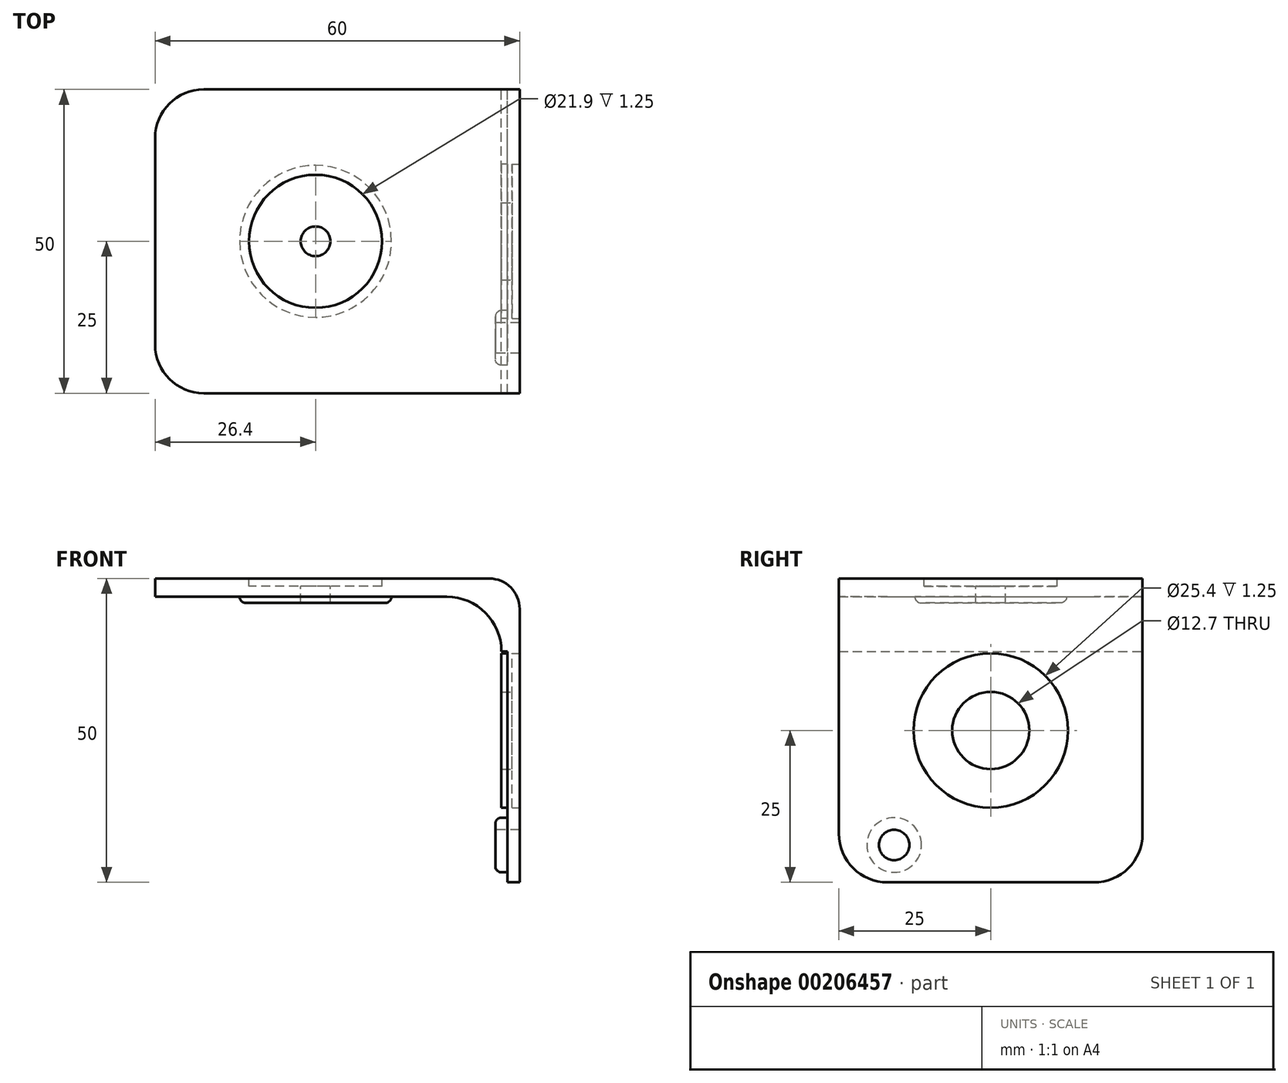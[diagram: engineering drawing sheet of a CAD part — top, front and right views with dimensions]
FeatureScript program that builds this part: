
annotation { "Feature Type Name" : "Feature", "Feature Type Description" : "" }
export const myFeature = defineFeature(function(context is Context, id is Id, definition is map)
    precondition{}
    {
        {
            var Q0;
            Q0=qCreatedBy(makeId("Front.planeOp"),FACE);
            var sketch = newSketch(context, id + "F0", { "sketchPlane" : qUnion([Q0])});
            skLineSegment(sketch, "E0.bottom", {"start": v(30, 25) * mm, "end": v(-30, 25) * mm});
            skLineSegment(sketch, "E0.top", {"start": v(30, -25) * mm, "end": v(27, -25) * mm});
            skLineSegment(sketch, "E0.left", {"start": v(30, 25) * mm, "end": v(30, -25) * mm});
            skLineSegment(sketch, "E0.right", {"start": v(-30, 25) * mm, "end": v(-30, 22) * mm});
            skPoint(sketch, "E0.middle", {"position": v(0, 0) * mm});
            skLineSegment(sketch, "E1", {"start": v(-30, 22) * mm, "end": v(18, 22) * mm});
            skLineSegment(sketch, "E2", {"start": v(27, 13) * mm, "end": v(27, -25) * mm});
            skPoint(sketch, "E3.orphan", {"position": v(-30, -25) * mm});
            skPoint(sketch, "E4.visualSharp", {"position": v(27, 22) * mm});
            skArc(sketch, "E4.filletArc", {"start": v(27, 13) * mm, "mid": v(24.36, 19.36) * mm, "end": v(18, 22) * mm});
            skSolve(sketch);
        }
        {
            var Q0;
            Q0=makeQuery(id+"F0.imprint","IMPRINT",FACE,{"disambiguationData":[TD([[makeQuery(id+"F0.imprint","IMPRINT",EDGE,{"derivedFrom":sQuery(id+"F0.wireOp",EDGE,"E0.bottom")}),1.0]])]});
            extrude(context, id + "F1", {"entities" : qUnion([Q0]), "endBound" : BoundingType.SYMMETRIC, "depth" : 50 * mm});
        }
        {
            var Q0;
            Q0=makeQuery(id+"F1.opExtrude","CAP_EDGE",EDGE,{"disambiguationData":[OSD([sQuery(id+"F0.wireOp",EDGE,"E0.right")])],"isStart":false});
            var Q1;
            Q1=makeQuery(id+"F1.opExtrude","CAP_EDGE",EDGE,{"disambiguationData":[OSD([sQuery(id+"F0.wireOp",EDGE,"E0.right")])],"isStart":true});
            var Q2;
            Q2=makeQuery(id+"F1.opExtrude","CAP_EDGE",EDGE,{"disambiguationData":[OSD([sQuery(id+"F0.wireOp",EDGE,"E0.top")])],"isStart":true});
            var Q3;
            Q3=makeQuery(id+"F1.opExtrude","CAP_EDGE",EDGE,{"disambiguationData":[OSD([sQuery(id+"F0.wireOp",EDGE,"E0.top")])],"isStart":false});
            fillet(context, id + "F2", {"entities" : qUnion([Q0, Q1, Q2, Q3]), "radius" : 8 * mm, "tangentPropagation" : true, "allowEdgeOverflow" : false});
        }
        {
            var Q0;
            Q0=makeQuery(id+"F1.opExtrude","SWEPT_FACE",FACE,{"disambiguationData":[OSD([sQuery(id+"F0.wireOp",EDGE,"E0.bottom")])]});
            var sketch = newSketch(context, id + "F3", { "sketchPlane" : qUnion([Q0])});
            skCircle(sketch, "E5", {"center": v(-3.6, 0) * mm, "radius": 10.95 * mm});
            skCircle(sketch, "E6", {"center": v(-3.6, 0) * mm, "radius": 2.45 * mm});
            skPoint(sketch, "E7.orphan", {"position": v(30, 0) * mm});
            skPoint(sketch, "E8.end.orphan", {"position": v(-30, 0) * mm});
            skSolve(sketch);
        }
        {
            var Q0;
            Q0=makeQuery(id+"F1.opExtrude","SWEPT_FACE",FACE,{"disambiguationData":[OSD([sQuery(id+"F0.wireOp",EDGE,"E0.left")])]});
            var sketch = newSketch(context, id + "F4", { "sketchPlane" : qUnion([Q0])});
            skCircle(sketch, "E9", {"center": v(0, 0) * mm, "radius": 12.7 * mm});
            skCircle(sketch, "E10", {"center": v(0, 0) * mm, "radius": 6.35 * mm});
            skPoint(sketch, "E11.orphan", {"position": v(0, 25) * mm});
            skPoint(sketch, "E12.end.orphan", {"position": v(0, -25) * mm});
            skSolve(sketch);
        }
        {
            var Q0;
            Q0=makeQuery(id+"F3.imprint","IMPRINT",FACE,{"disambiguationData":[TD([[makeQuery(id+"F3.imprint","IMPRINT",EDGE,{"derivedFrom":sQuery(id+"F3.wireOp",EDGE,"E5")}),1.0]])]});
            extrude(context, id + "F5", {"entities" : qUnion([Q0]), "operationType" : NewBodyOperationType.REMOVE, "oppositeDirection" : true, "depth" : 1.25 * mm});
        }
        {
            var Q0;
            Q0=makeQuery(id+"F5.boolean.opBoolean","SPLIT",FACE,{"disambiguationData":[TD([makeQuery(id+"F5.opExtrude","SWEPT_FACE",FACE,{"disambiguationData":[OSD([sQuery(id+"F3.wireOp",EDGE,"E6")])]})])],"derivedFrom":makeQuery(id+"F1.opExtrude","SWEPT_FACE",FACE,{"disambiguationData":[OSD([sQuery(id+"F0.wireOp",EDGE,"E0.bottom")])]})});
            extrude(context, id + "F6", {"entities" : qUnion([Q0]), "operationType" : NewBodyOperationType.REMOVE, "oppositeDirection" : true, "depth" : 3 * mm});
        }
        {
            var Q0;
            Q0=makeQuery(id+"F1.opExtrude","SWEPT_FACE",FACE,{"disambiguationData":[OSD([sQuery(id+"F0.wireOp",EDGE,"E2")])]});
            var sketch = newSketch(context, id + "F7", { "sketchPlane" : qUnion([Q0])});
            skCircle(sketch, "E13.0", {"center": v(0, 0) * mm, "radius": 12.7 * mm});
            skCircle(sketch, "E13.1", {"center": v(0, 0) * mm, "radius": 6.35 * mm});
            skLineSegment(sketch, "E14", {"start": v(0, -12.7) * mm, "end": v(0, -25) * mm});
            skCircle(sketch, "E15", {"center": v(15.9, -18.85) * mm, "radius": 2.5 * mm});
            skPoint(sketch, "E15.centerSnap0", {"position": v(0, -18.85) * mm});
            skCircle(sketch, "E16", {"center": v(15.9, -18.85) * mm, "radius": 4.5 * mm});
            skSolve(sketch);
        }
        {
            var Q0;
            Q0=makeQuery(id+"F4.imprint","IMPRINT",FACE,{"disambiguationData":[TD([[makeQuery(id+"F4.imprint","IMPRINT",EDGE,{"derivedFrom":sQuery(id+"F4.wireOp",EDGE,"E9")}),1.0]])]});
            extrude(context, id + "F8", {"entities" : qUnion([Q0]), "operationType" : NewBodyOperationType.REMOVE, "oppositeDirection" : true, "depth" : 1.25 * mm});
        }
        {
            var Q0;
            Q0=makeQuery(id+"F7.imprint","IMPRINT",FACE,{"disambiguationData":[TD([[makeQuery(id+"F7.imprint","IMPRINT",EDGE,{"derivedFrom":sQuery(id+"F7.wireOp",EDGE,"E13.0")}),-1.0]])]});
            extrude(context, id + "F9", {"entities" : qUnion([Q0]), "operationType" : NewBodyOperationType.REMOVE, "oppositeDirection" : true, "depth" : 1 * mm});
        }
        {
            var Q0;
            Q0=makeQuery(id+"F8.boolean.opBoolean","SPLIT",FACE,{"disambiguationData":[TD([makeQuery(id+"F8.opExtrude","SWEPT_FACE",FACE,{"disambiguationData":[OSD([sQuery(id+"F4.wireOp",EDGE,"E10")])]})])],"derivedFrom":makeQuery(id+"F1.opExtrude","SWEPT_FACE",FACE,{"disambiguationData":[OSD([sQuery(id+"F0.wireOp",EDGE,"E0.left")])]})});
            extrude(context, id + "F10", {"entities" : qUnion([Q0]), "operationType" : NewBodyOperationType.REMOVE, "oppositeDirection" : true, "depth" : 3 * mm});
        }
        {
            var Q0;
            Q0=makeQuery(id+"F1.opExtrude","SWEPT_EDGE",EDGE,{"disambiguationData":[OSD([sQuery(id+"F0.wireOp",EDGE,"E0.bottom"),sQuery(id+"F0.wireOp",EDGE,"E0.left")])]});
            fillet(context, id + "F11", {"entities" : qUnion([Q0]), "radius" : 5 * mm, "tangentPropagation" : true, "allowEdgeOverflow" : false});
        }
        {
            var Q0;
            Q0=makeQuery(id+"F7.imprint","IMPRINT",FACE,{"disambiguationData":[TD([[makeQuery(id+"F7.imprint","IMPRINT",EDGE,{"derivedFrom":sQuery(id+"F7.wireOp",EDGE,"E15")}),1.0]])]});
            var Q1;
            Q1=sQuery(id+"F7.wireOp",EDGE,"E15");
            extrude(context, id + "F12", {"entities" : qUnion([Q0]), "operationType" : NewBodyOperationType.REMOVE, "surfaceEntities" : qUnion([Q1]), "oppositeDirection" : true, "depth" : 3 * mm});
        }
        {
            var Q0;
            Q0=makeQuery(id+"F7.imprint","IMPRINT",FACE,{"disambiguationData":[TD([[makeQuery(id+"F7.imprint","IMPRINT",EDGE,{"derivedFrom":sQuery(id+"F7.wireOp",EDGE,"E15")}),-1.0]])]});
            extrude(context, id + "F13", {"entities" : qUnion([Q0]), "operationType" : NewBodyOperationType.ADD, "depth" : 1 * mm});
        }
        {
            var Q0;
            Q0=makeQuery(id+"F13.opExtrude","CAP_EDGE",EDGE,{"disambiguationData":[OSD([sQuery(id+"F7.wireOp",EDGE,"E16")])],"isStart":false});
            fillet(context, id + "F14", {"entities" : qUnion([Q0]), "radius" : 1 * mm, "tangentPropagation" : true, "allowEdgeOverflow" : false});
        }
        {
            var Q0;
            Q0=makeQuery(id+"F1.opExtrude","SWEPT_FACE",FACE,{"disambiguationData":[OSD([sQuery(id+"F0.wireOp",EDGE,"E1")])]});
            var sketch = newSketch(context, id + "F15", { "sketchPlane" : qUnion([Q0])});
            skCircle(sketch, "E17.0", {"center": v(-3.6, 0) * mm, "radius": 2.45 * mm});
            skCircle(sketch, "E18", {"center": v(-3.6, 0) * mm, "radius": 12.5 * mm});
            skSolve(sketch);
        }
        {
            var Q0;
            Q0=makeQuery(id+"F15.imprint","IMPRINT",FACE,{"disambiguationData":[TD([[makeQuery(id+"F15.imprint","IMPRINT",EDGE,{"derivedFrom":sQuery(id+"F15.wireOp",EDGE,"E17.0")}),1.0]])]});
            extrude(context, id + "F16", {"entities" : qUnion([Q0]), "operationType" : NewBodyOperationType.ADD, "depth" : 1 * mm});
        }
        {
            var Q0;
            Q0=makeQuery(id+"F16.opExtrude","CAP_EDGE",EDGE,{"disambiguationData":[OSD([sQuery(id+"F15.wireOp",EDGE,"E18")])],"isStart":false});
            fillet(context, id + "F17", {"entities" : qUnion([Q0]), "radius" : 1 * mm, "tangentPropagation" : true, "allowEdgeOverflow" : false});
        }
    });
